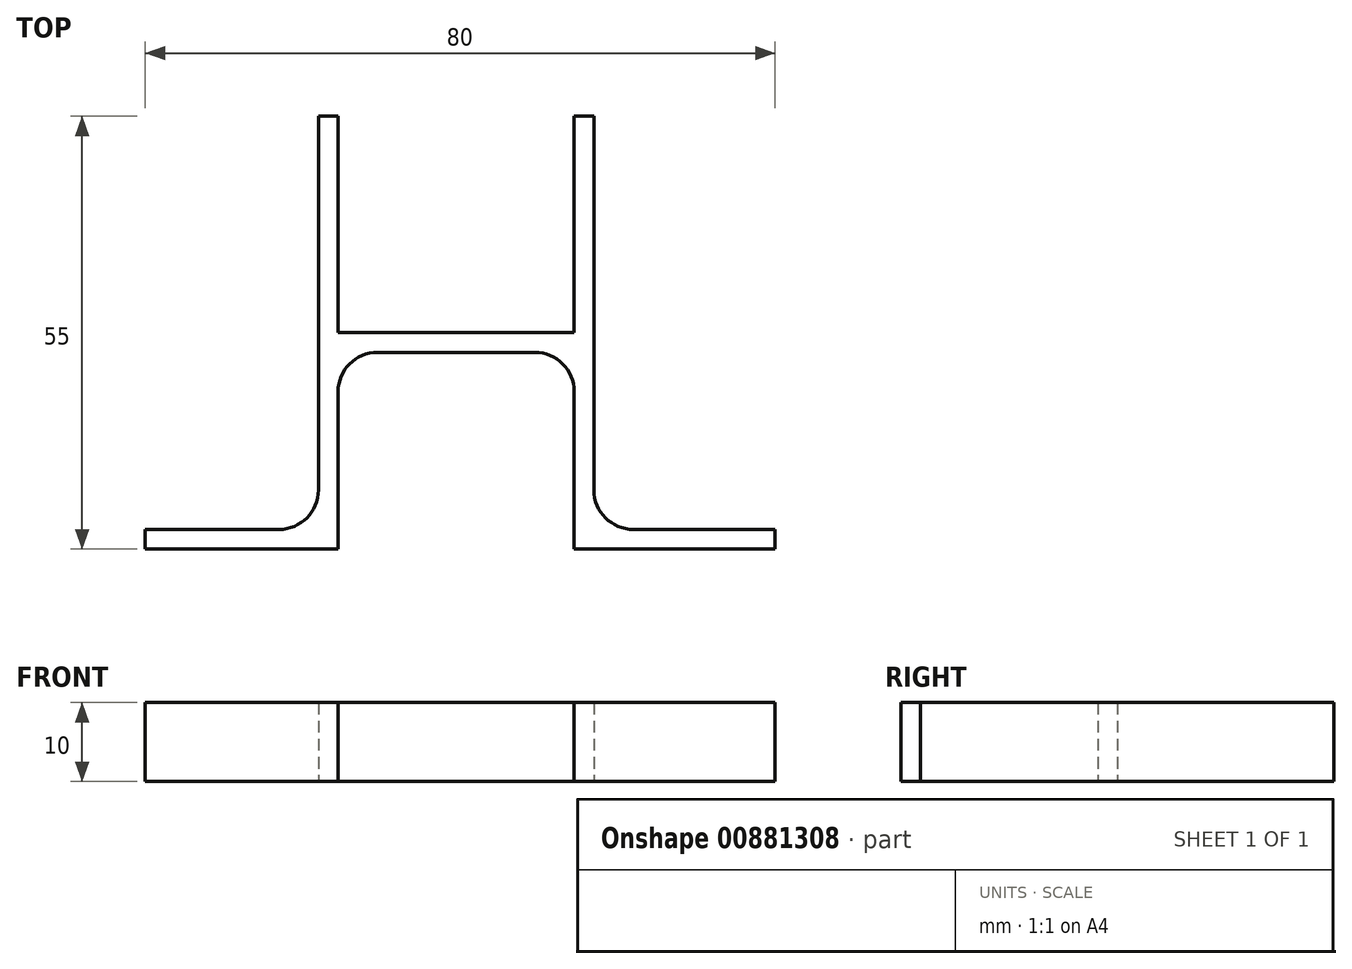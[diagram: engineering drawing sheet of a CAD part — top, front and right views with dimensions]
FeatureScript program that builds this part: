
annotation { "Feature Type Name" : "Feature", "Feature Type Description" : "" }
export const myFeature = defineFeature(function(context is Context, id is Id, definition is map)
    precondition{}
    {
        {
            var Q0;
            Q0=qCreatedBy(makeId("Top.planeOp"),FACE);
            var sketch = newSketch(context, id + "F0", { "sketchPlane" : qUnion([Q0])});
            skPoint(sketch, "E0", {"position": v(-15.5, 0) * mm});
            skPoint(sketch, "E1", {"position": v(14.5, 0) * mm});
            skPoint(sketch, "E2", {"position": v(-15.5, -25) * mm});
            skPoint(sketch, "E3", {"position": v(14.5, -25) * mm});
            skPoint(sketch, "E4", {"position": v(-15.5, 30) * mm});
            skPoint(sketch, "E5", {"position": v(14.5, 30) * mm});
            skPoint(sketch, "E6", {"position": v(40, -25) * mm});
            skPoint(sketch, "E7", {"position": v(-40, -25) * mm});
            skLineSegment(sketch, "E8", {"start": v(-15.5, 30) * mm, "end": v(-15.5, -25) * mm});
            skLineSegment(sketch, "E9", {"start": v(-40, -25) * mm, "end": v(-15.5, -25) * mm});
            skLineSegment(sketch, "E10", {"start": v(14.5, 30) * mm, "end": v(14.5, -25) * mm});
            skLineSegment(sketch, "E11", {"start": v(14.5, 0) * mm, "end": v(-15.5, 0) * mm});
            skLineSegment(sketch, "E12", {"start": v(14.5, -25) * mm, "end": v(40, -25) * mm});
            skPoint(sketch, "E13", {"position": v(-40, -22.5) * mm});
            skPoint(sketch, "E14", {"position": v(-15.5, -22.5) * mm});
            skPoint(sketch, "E15", {"position": v(14.5, -22.5) * mm});
            skPoint(sketch, "E16", {"position": v(40, -22.5) * mm});
            skPoint(sketch, "E17", {"position": v(17, -25) * mm});
            skPoint(sketch, "E18", {"position": v(17, 30) * mm});
            skPoint(sketch, "E19", {"position": v(-18, 30) * mm});
            skPoint(sketch, "E20", {"position": v(-18, -25) * mm});
            skLineSegment(sketch, "E21", {"start": v(-40, -25) * mm, "end": v(-40, -22.5) * mm});
            skLineSegment(sketch, "E22", {"start": v(-40, -22.5) * mm, "end": v(-15.5, -22.5) * mm});
            skLineSegment(sketch, "E23", {"start": v(-18, -25) * mm, "end": v(-18, 30) * mm});
            skLineSegment(sketch, "E24", {"start": v(17, 30) * mm, "end": v(17, -25) * mm});
            skLineSegment(sketch, "E25", {"start": v(14.5, -22.5) * mm, "end": v(40, -22.5) * mm});
            skLineSegment(sketch, "E26", {"start": v(40, -22.5) * mm, "end": v(40, -25) * mm});
            skPoint(sketch, "E27", {"position": v(-15.5, 2.5) * mm});
            skPoint(sketch, "E28", {"position": v(14.5, 2.5) * mm});
            skLineSegment(sketch, "E29", {"start": v(-15.5, 2.5) * mm, "end": v(14.5, 2.5) * mm});
            skLineSegment(sketch, "E30", {"start": v(-18, 30) * mm, "end": v(-15.5, 30) * mm});
            skLineSegment(sketch, "E31", {"start": v(14.5, 30) * mm, "end": v(17, 30) * mm});
            skSolve(sketch);
        }
        {
            var Q0;
            {var subQ3=sQuery(id+"F0.wireOp",EDGE,"E30");Q0=makeQuery(id+"F0.imprint","IMPRINT",FACE,{"disambiguationData":[TD([[makeQuery(id+"F0.imprint","IMPRINT",EDGE,{"derivedFrom":subQ3}),-1.0]])]});}
            var Q1;
            {var subQ0=sQuery(id+"F0.wireOp",EDGE,"E21");Q1=makeQuery(id+"F0.imprint","IMPRINT",FACE,{"disambiguationData":[TD([[makeQuery(id+"F0.imprint","IMPRINT",EDGE,{"derivedFrom":subQ0}),-1.0]])]});}
            var Q2;
            {var subQ0=sQuery(id+"F0.wireOp",EDGE,"E11");Q2=makeQuery(id+"F0.imprint","IMPRINT",FACE,{"disambiguationData":[TD([[makeQuery(id+"F0.imprint","IMPRINT",EDGE,{"derivedFrom":subQ0}),-1.0]])]});}
            var Q3;
            {var subQ0=sQuery(id+"F0.wireOp",EDGE,"E31");Q3=makeQuery(id+"F0.imprint","IMPRINT",FACE,{"disambiguationData":[TD([[makeQuery(id+"F0.imprint","IMPRINT",EDGE,{"derivedFrom":subQ0}),-1.0]])]});}
            var Q4;
            {var subQ3=sQuery(id+"F0.wireOp",EDGE,"E26");Q4=makeQuery(id+"F0.imprint","IMPRINT",FACE,{"disambiguationData":[TD([[makeQuery(id+"F0.imprint","IMPRINT",EDGE,{"derivedFrom":subQ3}),-1.0]])]});}
            var Q5;
            {var subQ0=sQuery(id+"F0.wireOp",EDGE,"E12");var subQ1=sQuery(id+"F0.wireOp",EDGE,"E10");var subQ2=makeQuery(id+"F0.imprint","INTERSECT",VERTEX,{"derivedFrom":[subQ1,subQ0]});Q5=makeQuery(id+"F0.imprint","IMPRINT",FACE,{"disambiguationData":[TD([[makeQuery(id+"F0.imprint","IMPRINT",EDGE,{"disambiguationData":[TD([[subQ2,1.0]])],"derivedFrom":subQ1}),1.0]])]});}
            var Q6;
            {var subQ0=sQuery(id+"F0.wireOp",EDGE,"E9");var subQ1=sQuery(id+"F0.wireOp",EDGE,"E8");var subQ2=makeQuery(id+"F0.imprint","INTERSECT",VERTEX,{"derivedFrom":[subQ1,subQ0]});Q6=makeQuery(id+"F0.imprint","IMPRINT",FACE,{"disambiguationData":[TD([[makeQuery(id+"F0.imprint","IMPRINT",EDGE,{"disambiguationData":[TD([[subQ2,1.0]])],"derivedFrom":subQ1}),-1.0]])]});}
            extrude(context, id + "F1", {"entities" : qUnion([Q0, Q1, Q2, Q3, Q4, Q5, Q6]), "depth" : 10 * mm, "offsetDistance" : 25 * mm});
        }
        {
            var Q0;
            Q0=makeQuery(id+"F1.opExtrude","SWEPT_EDGE",EDGE,{"disambiguationData":[OSD([sQuery(id+"F0.wireOp",EDGE,"E22"),sQuery(id+"F0.wireOp",EDGE,"E23")])]});
            var Q1;
            Q1=makeQuery(id+"F1.opExtrude","SWEPT_EDGE",EDGE,{"disambiguationData":[OSD([sQuery(id+"F0.wireOp",EDGE,"E24"),sQuery(id+"F0.wireOp",EDGE,"E25")])]});
            var Q2;
            Q2=makeQuery(id+"F1.opExtrude","SWEPT_EDGE",EDGE,{"disambiguationData":[OSD([sQuery(id+"F0.wireOp",EDGE,"E10"),sQuery(id+"F0.wireOp",EDGE,"E11")])]});
            var Q3;
            Q3=makeQuery(id+"F1.opExtrude","SWEPT_EDGE",EDGE,{"disambiguationData":[OSD([sQuery(id+"F0.wireOp",EDGE,"E8"),sQuery(id+"F0.wireOp",EDGE,"E11")])]});
            fillet(context, id + "F2", {"entities" : qUnion([Q0, Q1, Q2, Q3]), "tangentPropagation" : true, "radius" : 5 * mm, "defaultsChanged" : false, "vertexSettings" : [], "allowEdgeOverflow" : false});
        }
    });
